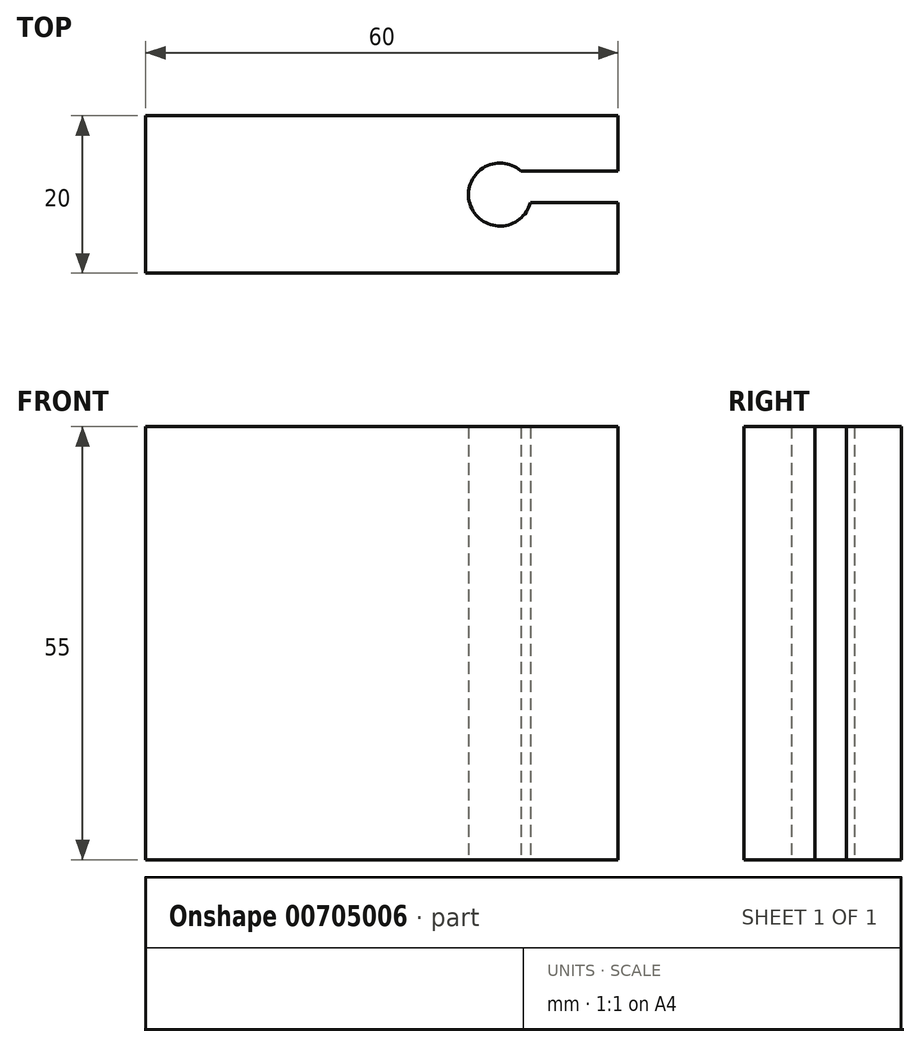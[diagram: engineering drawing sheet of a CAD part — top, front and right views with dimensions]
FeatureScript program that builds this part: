
annotation { "Feature Type Name" : "Feature", "Feature Type Description" : "" }
export const myFeature = defineFeature(function(context is Context, id is Id, definition is map)
    precondition{}
    {
        {
            var Q0;
            Q0=qCreatedBy(makeId("Front.planeOp"),FACE);
            var sketch = newSketch(context, id + "F0", { "sketchPlane" : qUnion([Q0])});
            skLineSegment(sketch, "E0.bottom", {"start": v(30, 27.5) * mm, "end": v(-30, 27.5) * mm});
            skLineSegment(sketch, "E0.top", {"start": v(30, -27.5) * mm, "end": v(-30, -27.5) * mm});
            skLineSegment(sketch, "E0.left", {"start": v(30, 27.5) * mm, "end": v(30, -27.5) * mm});
            skLineSegment(sketch, "E0.right", {"start": v(-30, 27.5) * mm, "end": v(-30, -27.5) * mm});
            skPoint(sketch, "E0.middle", {"position": v(0, 0) * mm});
            skSolve(sketch);
        }
        {
            var Q0;
            Q0=makeQuery(id+"F0.imprint","IMPRINT",FACE,{"disambiguationData":[TD([[makeQuery(id+"F0.imprint","IMPRINT",EDGE,{"derivedFrom":sQuery(id+"F0.wireOp",EDGE,"E0.bottom")}),1.0]])]});
            extrude(context, id + "F1", {"entities" : qUnion([Q0]), "depth" : 20 * mm, "offsetDistance" : 25 * mm});
        }
        {
            var Q0;
            Q0=makeQuery(id+"F1.opExtrude","SWEPT_FACE",FACE,{"disambiguationData":[OSD([sQuery(id+"F0.wireOp",EDGE,"E0.top")])]});
            var sketch = newSketch(context, id + "F2", { "sketchPlane" : qUnion([Q0])});
            skCircle(sketch, "E1", {"center": v(15, 10) * mm, "radius": 4 * mm});
            skLineSegment(sketch, "E2", {"start": v(12.35, 7) * mm, "end": v(30, 7) * mm});
            skLineSegment(sketch, "E3", {"start": v(18.87, 11) * mm, "end": v(30, 11) * mm});
            skSolve(sketch);
        }
        {
            var Q0;
            {var subQ0=sQuery(id+"F2.wireOp",EDGE,"E3");Q0=makeQuery(id+"F2.imprint","IMPRINT",FACE,{"disambiguationData":[TD([[makeQuery(id+"F2.imprint","IMPRINT",EDGE,{"derivedFrom":subQ0}),-1.0]])]});}
            var Q1;
            {var subQ0=sQuery(id+"F2.wireOp",EDGE,"E2");var subQ1=sQuery(id+"F2.wireOp",EDGE,"E1");var subQ2=makeQuery(id+"F2.imprint","INTERSECT",VERTEX,{"disambiguationData":[OD(0.0)],"derivedFrom":[subQ1,subQ0]});Q1=makeQuery(id+"F2.imprint","IMPRINT",FACE,{"disambiguationData":[TD([[makeQuery(id+"F2.imprint","IMPRINT",EDGE,{"disambiguationData":[TD([[subQ2,1.0]])],"derivedFrom":subQ1}),1.0]])]});}
            var Q2;
            {var subQ0=sQuery(id+"F2.wireOp",EDGE,"E2");var subQ1=sQuery(id+"F2.wireOp",EDGE,"E1");var subQ2=makeQuery(id+"F2.imprint","INTERSECT",VERTEX,{"disambiguationData":[OD(0.0)],"derivedFrom":[subQ1,subQ0]});Q2=makeQuery(id+"F2.imprint","IMPRINT",FACE,{"disambiguationData":[TD([[makeQuery(id+"F2.imprint","IMPRINT",EDGE,{"disambiguationData":[TD([[subQ2,-1.0]])],"derivedFrom":subQ1}),1.0]])]});}
            extrude(context, id + "F3", {"entities" : qUnion([Q0, Q1, Q2]), "operationType" : NewBodyOperationType.REMOVE, "endBound" : BoundingType.UP_TO_NEXT, "oppositeDirection" : true, "depth" : 25 * mm, "offsetDistance" : 25 * mm});
        }
    });
